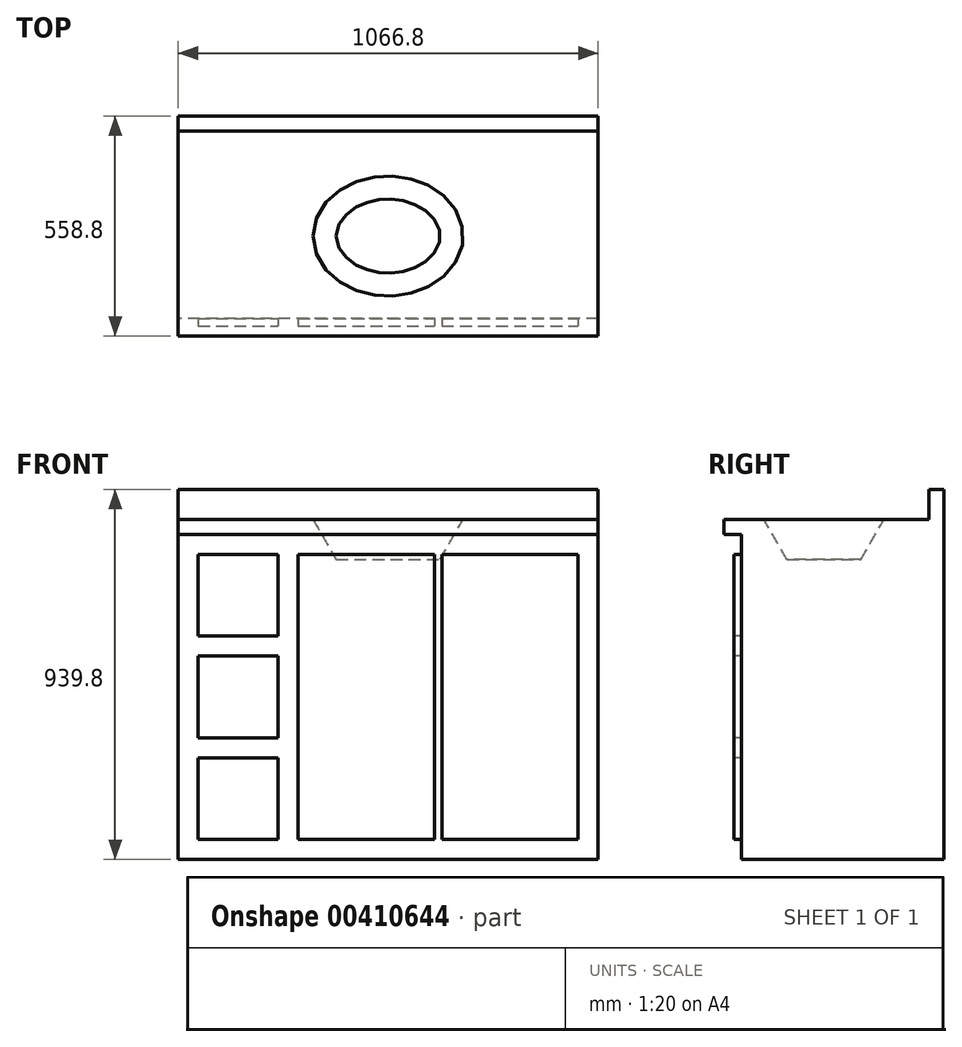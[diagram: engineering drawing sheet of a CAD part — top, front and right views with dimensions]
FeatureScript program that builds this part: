
annotation { "Feature Type Name" : "Feature", "Feature Type Description" : "" }
export const myFeature = defineFeature(function(context is Context, id is Id, definition is map)
    precondition{}
    {
        {
            var Q0;
            Q0=qCreatedBy(makeId("Top.planeOp"),FACE);
            var sketch = newSketch(context, id + "F0", { "sketchPlane" : qUnion([Q0])});
            skLineSegment(sketch, "E0.bottom", {"start": v(533.4, -266.7) * mm, "end": v(-533.4, -266.7) * mm});
            skLineSegment(sketch, "E0.top", {"start": v(533.4, 266.7) * mm, "end": v(-533.4, 266.7) * mm});
            skLineSegment(sketch, "E0.left", {"start": v(533.4, -266.7) * mm, "end": v(533.4, 266.7) * mm});
            skLineSegment(sketch, "E0.right", {"start": v(-533.4, -266.7) * mm, "end": v(-533.4, 266.7) * mm});
            skPoint(sketch, "E0.middle", {"position": v(0, 0) * mm});
            skSolve(sketch);
        }
        {
            var Q0;
            Q0 = qSketchRegion(id + "F0", true);
            extrude(context, id + "F1", {"entities" : qUnion([Q0]), "depth" : 825.5 * mm});
        }
        {
            var Q0;
            Q0=makeQuery(id+"F1.opExtrude","CAP_FACE",FACE,{"disambiguationData":[OSD([sQuery(id+"F0.wireOp",EDGE,"E0.bottom"),sQuery(id+"F0.wireOp",EDGE,"E0.top"),sQuery(id+"F0.wireOp",EDGE,"E0.left"),sQuery(id+"F0.wireOp",EDGE,"E0.right")])],"isStart":false});
            var sketch = newSketch(context, id + "F2", { "sketchPlane" : qUnion([Q0])});
            skLineSegment(sketch, "E1.bottom", {"start": v(-533.4, 266.7) * mm, "end": v(533.4, 266.7) * mm});
            skLineSegment(sketch, "E1.left", {"start": v(-533.4, 266.7) * mm, "end": v(-533.4, -292.1) * mm});
            skLineSegment(sketch, "E1.right", {"start": v(533.4, 266.7) * mm, "end": v(533.4, -292.1) * mm});
            skLineSegment(sketch, "E2", {"start": v(-533.4, -292.1) * mm, "end": v(533.4, -292.1) * mm});
            skSolve(sketch);
        }
        {
            var Q0;
            Q0 = qSketchRegion(id + "F2", true);
            extrude(context, id + "F3", {"entities" : qUnion([Q0]), "operationType" : NewBodyOperationType.ADD, "depth" : 38.1 * mm});
        }
        {
            var Q0;
            Q0=makeQuery(id+"F3.opExtrude","CAP_FACE",FACE,{"disambiguationData":[OSD([sQuery(id+"F2.wireOp",EDGE,"E1.bottom"),sQuery(id+"F2.wireOp",EDGE,"E1.top"),sQuery(id+"F2.wireOp",EDGE,"E1.left"),sQuery(id+"F2.wireOp",EDGE,"E1.right")])],"isStart":false});
            var sketch = newSketch(context, id + "F4", { "sketchPlane" : qUnion([Q0])});
            skLineSegment(sketch, "E3.bottom", {"start": v(-533.4, 266.7) * mm, "end": v(533.4, 266.7) * mm});
            skLineSegment(sketch, "E3.top", {"start": v(-533.4, 228.6) * mm, "end": v(533.4, 228.6) * mm});
            skLineSegment(sketch, "E3.left", {"start": v(-533.4, 266.7) * mm, "end": v(-533.4, 228.6) * mm});
            skLineSegment(sketch, "E3.right", {"start": v(533.4, 266.7) * mm, "end": v(533.4, 228.6) * mm});
            skSolve(sketch);
        }
        {
            var Q0;
            Q0 = qSketchRegion(id + "F4", true);
            extrude(context, id + "F5", {"entities" : qUnion([Q0]), "operationType" : NewBodyOperationType.ADD, "depth" : 76.2 * mm});
        }
        {
            var Q0;
            Q0=makeQuery(id+"F1.opExtrude","SWEPT_FACE",FACE,{"disambiguationData":[OSD([sQuery(id+"F0.wireOp",EDGE,"E0.bottom")])]});
            var sketch = newSketch(context, id + "F6", { "sketchPlane" : qUnion([Q0])});
            skLineSegment(sketch, "E4.bottom", {"start": v(-482.6, 774.7) * mm, "end": v(-279.4, 774.7) * mm});
            skLineSegment(sketch, "E4.top", {"start": v(-482.6, 567.27) * mm, "end": v(-279.4, 567.27) * mm});
            skLineSegment(sketch, "E4.left", {"start": v(-482.6, 774.7) * mm, "end": v(-482.6, 567.27) * mm});
            skLineSegment(sketch, "E4.right", {"start": v(-279.4, 774.7) * mm, "end": v(-279.4, 567.27) * mm});
            skLineSegment(sketch, "E5.bottom", {"start": v(-482.6, 516.47) * mm, "end": v(-279.4, 516.47) * mm});
            skLineSegment(sketch, "E5.top", {"start": v(-482.6, 309.03) * mm, "end": v(-279.4, 309.03) * mm});
            skLineSegment(sketch, "E5.left", {"start": v(-482.6, 516.47) * mm, "end": v(-482.6, 309.03) * mm});
            skLineSegment(sketch, "E5.right", {"start": v(-279.4, 516.47) * mm, "end": v(-279.4, 309.03) * mm});
            skLineSegment(sketch, "E6.bottom", {"start": v(-482.6, 258.23) * mm, "end": v(-279.4, 258.23) * mm});
            skLineSegment(sketch, "E6.top", {"start": v(-482.6, 50.8) * mm, "end": v(-279.4, 50.8) * mm});
            skLineSegment(sketch, "E6.left", {"start": v(-482.6, 258.23) * mm, "end": v(-482.6, 50.8) * mm});
            skLineSegment(sketch, "E6.right", {"start": v(-279.4, 258.23) * mm, "end": v(-279.4, 50.8) * mm});
            skLineSegment(sketch, "E7.top", {"start": v(-228.6, 50.8) * mm, "end": v(117.48, 50.8) * mm});
            skLineSegment(sketch, "E7.left", {"start": v(-228.6, 774.7) * mm, "end": v(-228.6, 50.8) * mm});
            skLineSegment(sketch, "E7.right", {"start": v(117.48, 774.7) * mm, "end": v(117.48, 50.8) * mm});
            skLineSegment(sketch, "E8", {"start": v(-228.6, 774.7) * mm, "end": v(117.48, 774.7) * mm});
            skLineSegment(sketch, "E9.bottom", {"start": v(136.53, 774.7) * mm, "end": v(482.6, 774.7) * mm});
            skLineSegment(sketch, "E9.top", {"start": v(136.53, 50.8) * mm, "end": v(482.6, 50.8) * mm});
            skLineSegment(sketch, "E9.left", {"start": v(136.53, 774.7) * mm, "end": v(136.53, 50.8) * mm});
            skLineSegment(sketch, "E9.right", {"start": v(482.6, 774.7) * mm, "end": v(482.6, 50.8) * mm});
            skLineSegment(sketch, "E10.bottom", {"start": v(-533.4, 825.5) * mm, "end": v(533.4, 825.5) * mm});
            skLineSegment(sketch, "E10.left", {"start": v(-533.4, 825.5) * mm, "end": v(-533.4, 0) * mm});
            skLineSegment(sketch, "E10.right", {"start": v(533.4, 825.5) * mm, "end": v(533.4, 0) * mm});
            skLineSegment(sketch, "E11.right", {"start": v(533.4, 0) * mm, "end": v(-533.4, 0) * mm});
            skLineSegment(sketch, "E12", {"start": v(-381, 309.03) * mm, "end": v(-381, 258.23) * mm, "construction": true});
            skLineSegment(sketch, "E13", {"start": v(-381, 567.27) * mm, "end": v(-381, 516.47) * mm, "construction": true});
            skLineSegment(sketch, "E14", {"start": v(-279.4, 774.7) * mm, "end": v(-228.6, 774.7) * mm, "construction": true});
            skSolve(sketch);
        }
        {
            var Q0;
            Q0=makeQuery(id+"F6.imprint","IMPRINT",FACE,{"disambiguationData":[TD([[makeQuery(id+"F6.imprint","IMPRINT",EDGE,{"derivedFrom":sQuery(id+"F6.wireOp",EDGE,"E4.bottom")}),1.0]])]});
            extrude(context, id + "F7", {"entities" : qUnion([Q0]), "operationType" : NewBodyOperationType.REMOVE, "oppositeDirection" : true, "depth" : 19.05 * mm});
        }
        {
            var Q0;
            Q0=makeQuery(id+"F3.opExtrude","CAP_FACE",FACE,{"disambiguationData":[OSD([sQuery(id+"F2.wireOp",EDGE,"E1.bottom"),sQuery(id+"F2.wireOp",EDGE,"E1.left"),sQuery(id+"F2.wireOp",EDGE,"E1.right"),sQuery(id+"F2.wireOp",EDGE,"E2")])],"isStart":false});
            var sketch = newSketch(context, id + "F8", { "sketchPlane" : qUnion([Q0])});
            skEllipse(sketch, "E15", {"center": v(0, -38.1) * mm, "majorRadius": 190.5 * mm, "minorRadius": 152.4 * mm, "majorAxis": v(1, 0)});
            skLineSegment(sketch, "E16", {"start": v(0, 114.3) * mm, "end": v(0, -190.5) * mm, "construction": true});
            skLineSegment(sketch, "E17", {"start": v(-190.5, -38.1) * mm, "end": v(190.5, -38.1) * mm, "construction": true});
            skSolve(sketch);
        }
        {
            var Q0;
            Q0 = qSketchRegion(id + "F8", true);
            extrude(context, id + "F9", {"entities" : qUnion([Q0]), "operationType" : NewBodyOperationType.REMOVE, "oppositeDirection" : true, "depth" : 101.6 * mm, "hasDraft" : true, "draftAngle" : 30 * degree, "draftPullDirection" : true});
        }
    });
